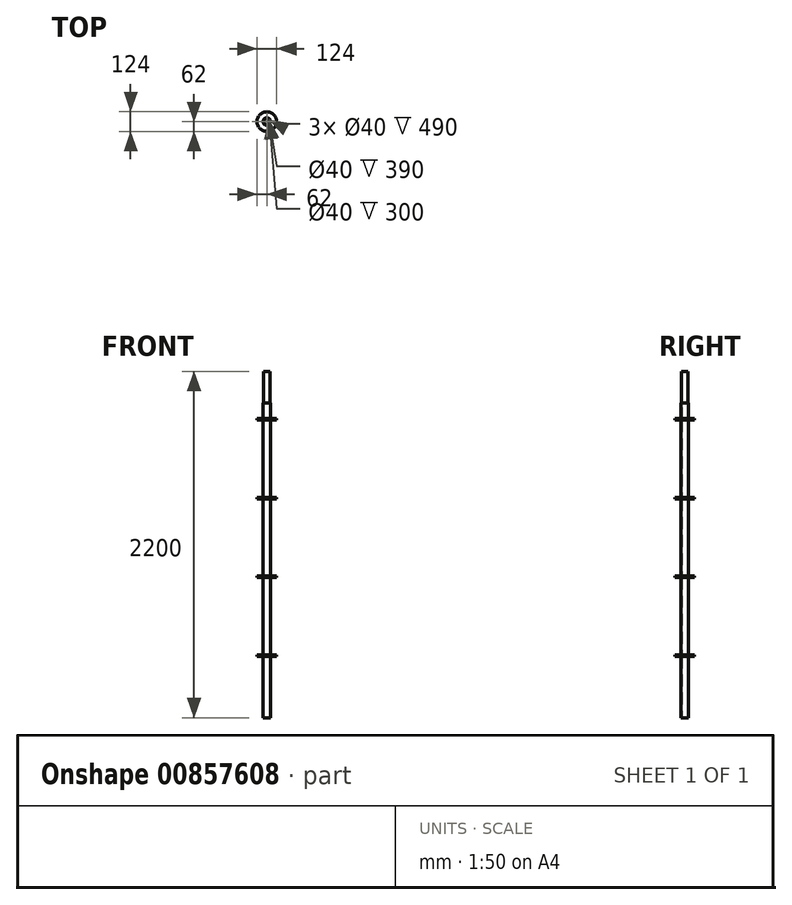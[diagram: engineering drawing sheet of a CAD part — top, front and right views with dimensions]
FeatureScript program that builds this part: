
annotation { "Feature Type Name" : "Feature", "Feature Type Description" : "" }
export const myFeature = defineFeature(function(context is Context, id is Id, definition is map)
    precondition{}
    {
        {
            var Q0;
            Q0=qCreatedBy(makeId("Front.planeOp"),FACE);
            var sketch = newSketch(context, id + "F0", { "sketchPlane" : qUnion([Q0])});
            skLineSegment(sketch, "E0", {"start": v(0, 0) * mm, "end": v(0, 2200) * mm, "construction": true});
            skLineSegment(sketch, "E1", {"start": v(20, 0) * mm, "end": v(20, 2200) * mm});
            skLineSegment(sketch, "E2", {"start": v(20, 0) * mm, "end": v(24.15, 0) * mm});
            skLineSegment(sketch, "E3", {"start": v(20, 400) * mm, "end": v(20, 1501.38) * mm});
            skLineSegment(sketch, "E4", {"start": v(24.15, 0) * mm, "end": v(24.15, 2000) * mm});
            skLineSegment(sketch, "E5", {"start": v(21, 2200) * mm, "end": v(20, 2200) * mm});
            skLineSegment(sketch, "E6", {"start": v(21, 2200) * mm, "end": v(21, 2000) * mm});
            skLineSegment(sketch, "E7", {"start": v(21, 2000) * mm, "end": v(24.15, 2000) * mm});
            skPoint(sketch, "E8.orphan", {"position": v(24.15, 2200) * mm});
            skSolve(sketch);
        }
        {
            var Q0;
            Q0 = qSketchRegion(id + "F0", true);
            var Q1;
            Q1=sQuery(id+"F0.wireOp",EDGE,"E0");
            revolve(context, id + "F1", {"surfaceOperationType" : NewSurfaceOperationType.NEW, "entities" : qUnion([Q0]), "axis" : qUnion([Q1]), "revolveType" : RevolveType.FULL});
        }
        {
            var Q0;
            Q0=qCreatedBy(makeId("Front.planeOp"),FACE);
            var sketch = newSketch(context, id + "F2", { "sketchPlane" : qUnion([Q0])});
            skLineSegment(sketch, "E9", {"start": v(0, 0) * mm, "end": v(0, 395) * mm, "construction": true});
            skLineSegment(sketch, "E10", {"start": v(0, 400) * mm, "end": v(62, 400) * mm});
            skLineSegment(sketch, "E11", {"start": v(62, 400) * mm, "end": v(62, 390) * mm});
            skLineSegment(sketch, "E12", {"start": v(62, 390) * mm, "end": v(0, 390) * mm});
            skLineSegment(sketch, "E13", {"start": v(0, 390) * mm, "end": v(0, 400) * mm});
            skLineSegment(sketch, "E14", {"start": v(0, 395) * mm, "end": v(0, 2001.17) * mm, "construction": true});
            skLineSegment(sketch, "E15.bottom", {"start": v(0, 890) * mm, "end": v(62, 890) * mm});
            skLineSegment(sketch, "E15.top", {"start": v(0, 900) * mm, "end": v(62, 900) * mm});
            skLineSegment(sketch, "E15.left", {"start": v(0, 890) * mm, "end": v(0, 900) * mm});
            skLineSegment(sketch, "E15.right", {"start": v(62, 890) * mm, "end": v(62, 900) * mm});
            skLineSegment(sketch, "E16.bottom", {"start": v(0, 1390) * mm, "end": v(62, 1390) * mm});
            skLineSegment(sketch, "E16.top", {"start": v(0, 1400) * mm, "end": v(62, 1400) * mm});
            skLineSegment(sketch, "E16.left", {"start": v(0, 1390) * mm, "end": v(0, 1400) * mm});
            skLineSegment(sketch, "E16.right", {"start": v(62, 1390) * mm, "end": v(62, 1400) * mm});
            skLineSegment(sketch, "E17.bottom", {"start": v(0, 1890) * mm, "end": v(62, 1890) * mm});
            skLineSegment(sketch, "E17.top", {"start": v(0, 1900) * mm, "end": v(62, 1900) * mm});
            skLineSegment(sketch, "E17.left", {"start": v(0, 1890) * mm, "end": v(0, 1900) * mm});
            skLineSegment(sketch, "E17.right", {"start": v(62, 1890) * mm, "end": v(62, 1900) * mm});
            skSolve(sketch);
        }
        {
            var Q0;
            Q0 = qSketchRegion(id + "F2", true);
            var Q1;
            Q1=sQuery(id+"F2.wireOp",EDGE,"E9");
            revolve(context, id + "F3", {"operationType" : NewBodyOperationType.ADD, "surfaceOperationType" : NewSurfaceOperationType.NEW, "entities" : qUnion([Q0]), "axis" : qUnion([Q1]), "revolveType" : RevolveType.FULL});
        }
    });
